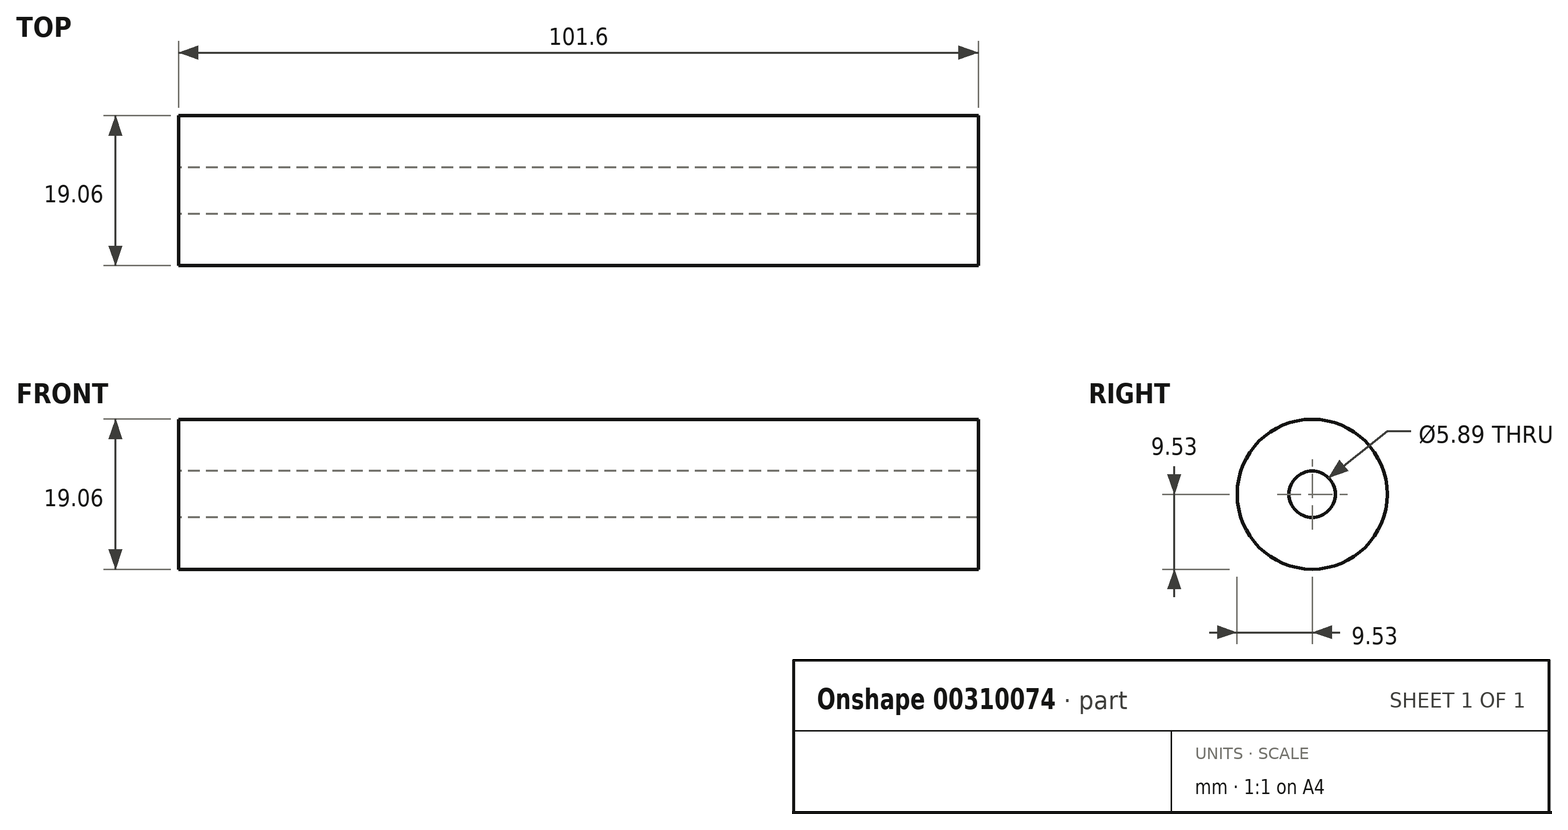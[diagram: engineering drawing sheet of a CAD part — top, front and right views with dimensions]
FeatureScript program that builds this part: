
annotation { "Feature Type Name" : "Feature", "Feature Type Description" : "" }
export const myFeature = defineFeature(function(context is Context, id is Id, definition is map)
    precondition{}
    {
        {
            var Q0;
            Q0=qCreatedBy(makeId("Right.planeOp"),FACE);
            var sketch = newSketch(context, id + "F0", { "sketchPlane" : qUnion([Q0])});
            skCircle(sketch, "E0", {"center": v(0, 0) * mm, "radius": 2.94 * mm});
            skCircle(sketch, "E1", {"center": v(0, 0) * mm, "radius": 9.53 * mm});
            skSolve(sketch);
        }
        {
            var Q0;
            Q0 = qSketchRegion(id + "F0", true);
            extrude(context, id + "F1", {"entities" : qUnion([Q0]), "flatOperationType" : FlatOperationType.REMOVE, "endBound" : BoundingType.SYMMETRIC, "offsetDistance" : 25.4 * mm, "depth" : 101.6 * mm, "domain" : OperationDomain.MODEL});
        }
    });
